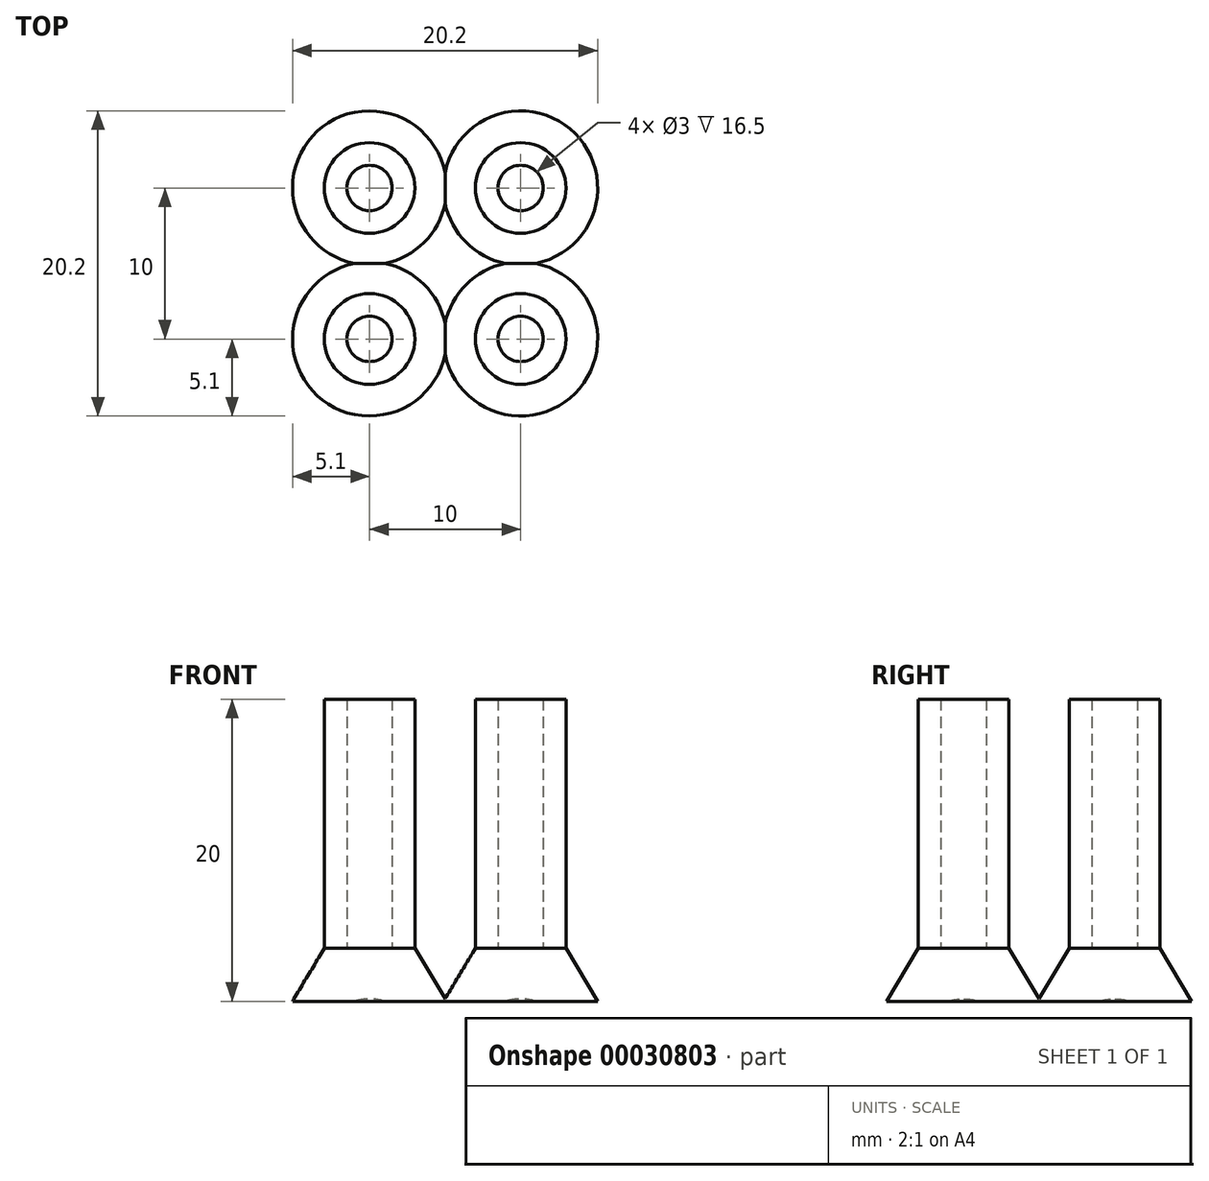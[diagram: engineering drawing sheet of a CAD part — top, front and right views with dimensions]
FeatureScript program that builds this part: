
annotation { "Feature Type Name" : "Feature", "Feature Type Description" : "" }
export const myFeature = defineFeature(function(context is Context, id is Id, definition is map)
    precondition{}
    {
        {
            var Q0;
            Q0=qCreatedBy(makeId("Top.planeOp"),FACE);
            var sketch = newSketch(context, id + "F0", { "sketchPlane" : qUnion([Q0])});
            skCircle(sketch, "E0", {"center": v(0, 0) * mm, "radius": 1.5 * mm});
            skCircle(sketch, "E1", {"center": v(0, 0) * mm, "radius": 3 * mm});
            skLineSegment(sketch, "E2", {"start": v(0, 0) * mm, "end": v(0, -5) * mm, "construction": true});
            skLineSegment(sketch, "E3", {"start": v(0, -5) * mm, "end": v(-5, -5) * mm, "construction": true});
            skLineSegment(sketch, "E4", {"start": v(-5, -5) * mm, "end": v(-5, 0) * mm, "construction": true});
            skCircle(sketch, "E5.MirrorC", {"center": v(-10, 0) * mm, "radius": 1.5 * mm});
            skCircle(sketch, "E6.MirrorC", {"center": v(-10, 0) * mm, "radius": 3 * mm});
            skCircle(sketch, "E7.MirrorC", {"center": v(-10, -10) * mm, "radius": 1.5 * mm});
            skCircle(sketch, "E8.MirrorC", {"center": v(-10, -10) * mm, "radius": 3 * mm});
            skCircle(sketch, "E9.MirrorC", {"center": v(0, -10) * mm, "radius": 1.5 * mm});
            skCircle(sketch, "E10.MirrorC", {"center": v(0, -10) * mm, "radius": 3 * mm});
            skSolve(sketch);
        }
        {
            var Q0;
            Q0=qSketchRegion(id+"F0",true);
            extrude(context, id + "F1", {"entities" : qUnion([Q0]), "depth" : 20 * mm});
        }
        {
            var Q0;
            Q0=qCreatedBy(makeId("Right.planeOp"),FACE);
            var sketch = newSketch(context, id + "F2", { "sketchPlane" : qUnion([Q0])});
            skLineSegment(sketch, "E11", {"start": v(0, 0) * mm, "end": v(-10, 0) * mm});
            skLineSegment(sketch, "E12", {"start": v(-5, 0) * mm, "end": v(-5, 3.5) * mm});
            skLineSegment(sketch, "E13", {"start": v(0, 0) * mm, "end": v(0, 3.5) * mm});
            skLineSegment(sketch, "E14", {"start": v(0, 3.5) * mm, "end": v(3, 3.5) * mm});
            skLineSegment(sketch, "E15", {"start": v(3, 3.5) * mm, "end": v(5.1, 0) * mm});
            skLineSegment(sketch, "E16", {"start": v(5.1, 0) * mm, "end": v(0, 0) * mm});
            skLineSegment(sketch, "E17.MirrorCS", {"start": v(-10, 0) * mm, "end": v(-10, 3.5) * mm});
            skLineSegment(sketch, "E18.MirrorCS", {"start": v(-10, 3.5) * mm, "end": v(-13, 3.5) * mm});
            skLineSegment(sketch, "E19.MirrorCS", {"start": v(-13, 3.5) * mm, "end": v(-15.1, 0) * mm});
            skLineSegment(sketch, "E20.MirrorCS", {"start": v(-15.1, 0) * mm, "end": v(-10, 0) * mm});
            skSolve(sketch);
        }
        {
            var Q0;
            Q0=makeQuery(id+"F2.imprint","IMPRINT",FACE,{"disambiguationData":[TD([[makeQuery(id+"F2.imprint","IMPRINT",EDGE,{"derivedFrom":sQuery(id+"F2.wireOp",EDGE,"E13")}),-1.0]])]});
            var Q1;
            Q1=sQuery(id+"F2.wireOp",EDGE,"E13");
            revolve(context, id + "F3", {"operationType" : NewBodyOperationType.ADD, "entities" : qUnion([Q0]), "axis" : qUnion([Q1]), "revolveType" : RevolveType.FULL});
        }
        {
            var Q0;
            Q0=makeQuery(id+"F2.imprint","IMPRINT",FACE,{"disambiguationData":[TD([[makeQuery(id+"F2.imprint","IMPRINT",EDGE,{"derivedFrom":sQuery(id+"F2.wireOp",EDGE,"E17.MirrorCS")}),1.0]])]});
            var Q1;
            Q1=sQuery(id+"F2.wireOp",EDGE,"E17.MirrorCS");
            revolve(context, id + "F4", {"operationType" : NewBodyOperationType.ADD, "entities" : qUnion([Q0]), "axis" : qUnion([Q1]), "revolveType" : RevolveType.FULL});
        }
        {
            var Q0;
            Q0=qCreatedBy(makeId("Right.planeOp"),FACE);
            cPlane(context, id + "F5", {"entities" : qUnion([Q0]), "cplaneType" : CPlaneType.OFFSET, "offset" : 10 * mm, "oppositeDirection" : true, "width" : 150 * mm, "height" : 150 * mm});
        }
        {
            var Q0;
            Q0=qCreatedBy(id+"F5.planeOp",FACE);
            var sketch = newSketch(context, id + "F6", { "sketchPlane" : qUnion([Q0])});
            skLineSegment(sketch, "E21", {"start": v(0, 0) * mm, "end": v(0, 3.5) * mm});
            skLineSegment(sketch, "E22", {"start": v(0, 0) * mm, "end": v(-5, 0) * mm, "construction": true});
            skLineSegment(sketch, "E23", {"start": v(-5, 0) * mm, "end": v(-5, 3.5) * mm, "construction": true});
            skLineSegment(sketch, "E24", {"start": v(0, 3.5) * mm, "end": v(3, 3.5) * mm});
            skLineSegment(sketch, "E25", {"start": v(3, 3.5) * mm, "end": v(5.1, 0) * mm});
            skLineSegment(sketch, "E26", {"start": v(5.1, 0) * mm, "end": v(0, 0) * mm});
            skLineSegment(sketch, "E27.MirrorCS", {"start": v(-10, 0) * mm, "end": v(-10, 3.5) * mm});
            skLineSegment(sketch, "E28.MirrorCS", {"start": v(-10, 3.5) * mm, "end": v(-13, 3.5) * mm});
            skLineSegment(sketch, "E29.MirrorCS", {"start": v(-13, 3.5) * mm, "end": v(-15.1, 0) * mm});
            skLineSegment(sketch, "E30.MirrorCS", {"start": v(-15.1, 0) * mm, "end": v(-10, 0) * mm});
            skSolve(sketch);
        }
        {
            var Q0;
            Q0=makeQuery(id+"F6.imprint","IMPRINT",FACE,{"disambiguationData":[TD([[makeQuery(id+"F6.imprint","IMPRINT",EDGE,{"derivedFrom":sQuery(id+"F6.wireOp",EDGE,"E21")}),-1.0]])]});
            var Q1;
            Q1=sQuery(id+"F6.wireOp",EDGE,"E21");
            revolve(context, id + "F7", {"operationType" : NewBodyOperationType.ADD, "entities" : qUnion([Q0]), "axis" : qUnion([Q1]), "revolveType" : RevolveType.FULL});
        }
        {
            var Q0;
            Q0=makeQuery(id+"F6.imprint","IMPRINT",FACE,{"disambiguationData":[TD([[makeQuery(id+"F6.imprint","IMPRINT",EDGE,{"derivedFrom":sQuery(id+"F6.wireOp",EDGE,"E27.MirrorCS")}),1.0]])]});
            var Q1;
            Q1=sQuery(id+"F6.wireOp",EDGE,"E27.MirrorCS");
            revolve(context, id + "F8", {"operationType" : NewBodyOperationType.ADD, "entities" : qUnion([Q0]), "axis" : qUnion([Q1]), "revolveType" : RevolveType.FULL});
        }
    });
